# Revit family: Gira_5532902
name_source: partatom
category: Electrical Fixtures
revit_build: Autodesk Revit 2017 (Build: 20160225_1515(x64)
units: mm (PartAtom-declared; Revit-internal decimal feet)

## family parameters
Cut with Voids When Loaded = No
Host = Face
Maintain Annotation Orientation = Yes
Part Type = Normal
Room Calculation Point = No
Round Connector Dimension = Use Diameter
Shared = No

## types (1)
- Call-btn mod.2-g System 106 traffic white(lac.)
    Available = No
    BIM (1) = https://media.stage.bim.site und Tasten.rfa?public/gira/36a6b08/Sys106_Abdeckung_Schalten und Tasten.rfa
    Category = Functional module for door communication
    Colour = White
    Data sheet (1) = https://katalog.gira.de
    Default Elevation = 1219 mm
    Description = C.btn mod.2g S106 TWl,System 106 call-button module,2-gang,Traffic white (laquered),The Gira System 106 is an installation system made of metal in a puristic and elegant frameless design, based on basic measurements of 106.5 × 106.5 mm. With the modular door intercom in Gira System 106, hospitality begins even before you reach the front door. All the functions are presented in a harmonious overall appearance, from the call button module, intercom module, and camera module, up to the info and blank module. In the dark, backlit call buttons with inscription space ensure good legibility and an attractive appearance.,,Individually adaptable modular system, The System 106 can be used in family homes or apartment buildings, as well as in office buildings, industrial properties, and hotels. The modular design enables the system's size, design, and functionality to be individually adapted to the respective requirements. Expansions and changes are possible at any time by easily exchanging the modules.,With this system, it is also possible to exchange the fronts only. This means that the appearance of the system can be changed from e.g. traffic white to a stainless steel surface at a later stage, without having to exchange the electronic units.,,High-quality materials,The modules are frameless with design fronts made of genuine materials, available in two brushed stainless steel versions (V2A and V4A), anodised aluminium C-0, and a metal alloy lacquered in traffic white (RAL 9016): all robust materials which ensure durability. The camera and DIN 18040 display module feature a black glass cover.,,Easy and phased installation,The system can be installed in phases, in parallel to the progress of building work. In this way, it is possible to initially install only the lower part of a surface-mounted housing during construction of the shell; cables and modules can then be added when they are needed.,,Individual inscription options,Call button modules and info modules can be labelled individually via the Gira inscription service.,,Features:,- Easy-to-use, vandal-proof, and scratch-resistant call buttons.,- Function changes, e.g. from 2-gang to 4-gang, can be easily realised by replacing the buttons.,- Various inscription options possible.,,Notes :,- Professional labelling with the Gira Inscription Service www.marking.gira.com.
    GTIN = 4010337022572
    HAN = 5532902
    Height = 0.1065
    HeinzeBIM = https://bimportal.heinze.de
    Installation technique = Bus system
    Manufacturer = Gira
    Manufacturer URL = https://www.gira.de
    Model = Sys106_Abdeckung_Schalten und Tasten
    Name = Call-btn mod.2-g System 106 traffic white(lac.)
    Number of bell buttons = 2
    URL = http://katalog.gira.de
    Width = 0.1065

## geometry (parser evidence)
native form markers: Sweep x4
no freeform markers — native parametric forms only
